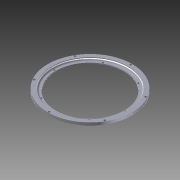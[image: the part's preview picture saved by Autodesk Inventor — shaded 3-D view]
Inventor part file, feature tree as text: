
AUTODESK INVENTOR PART (.ipt)
format: ipt  version: 2014 SP1 (Build 180222100, 222)  size: 822,272 bytes
history: native  units: in
note: dims shown in document units (in); Inventor stores cm internally (conversion verified against a paired STEP export)
features: other x7, plane x5
ambient origin geometry x8: Origin, YZ Plane, XZ Plane, XY Plane, X Axis, Y Axis, Z Axis, Center Point
bodies: Body1 (feature_tree), Body2 (feature_tree), Body3 (feature_tree), Body4 (feature_tree), Body5 (feature_tree), Body6 (feature_tree), Body7 (feature_tree), Body8 (feature_tree), Body9 (feature_tree), Body10 (feature_tree), Body11 (feature_tree), Body12 (feature_tree), Body13 (feature_tree), Body14 (feature_tree), Body15 (feature_tree), Body16 (feature_tree), Body17 (feature_tree), Body18 (feature_tree), Body19 (feature_tree), Body20 (feature_tree), Body21 (feature_tree), Body22 (feature_tree), Body23 (feature_tree), Body24 (feature_tree), Body25 (feature_tree), Body26 (feature_tree), Body27 (feature_tree), Body28 (feature_tree), Body29 (feature_tree), Body30 (feature_tree), Body31 (feature_tree), Body32 (feature_tree), Body33 (feature_tree), Body34 (feature_tree), Body35 (feature_tree), Body36 (feature_tree), Body37 (feature_tree), Body38 (feature_tree), Body39 (feature_tree), Body40 (feature_tree), Body41 (feature_tree), Body42 (feature_tree), Body43 (feature_tree), Body44 (feature_tree), Body45 (feature_tree), Body46 (feature_tree), Body47 (feature_tree), Body48 (feature_tree), Body49 (feature_tree), Body50 (feature_tree), Body51 (feature_tree), Body52 (feature_tree), Body53 (feature_tree), Body54 (feature_tree), Body55 (feature_tree), Body56 (feature_tree), Body57 (feature_tree), Body58 (feature_tree), Body59 (feature_tree), Body60 (feature_tree), Body61 (feature_tree), Body62 (feature_tree), Body63 (feature_tree), Body64 (feature_tree), Body65 (feature_tree), Body66 (feature_tree), Body67 (feature_tree), Body68 (feature_tree), Body69 (feature_tree), Body70 (feature_tree), Body71 (feature_tree), Body72 (feature_tree), Body73 (feature_tree), Body74 (feature_tree), Body75 (feature_tree), Body76 (feature_tree), Body77 (feature_tree), Body78 (feature_tree), Body79 (feature_tree), Body80 (feature_tree), Body81 (feature_tree), Body82 (feature_tree), Body83 (feature_tree), Body84 (feature_tree), Body85 (feature_tree), Body86 (feature_tree), Body87 (feature_tree), Body88 (feature_tree), Body89 (feature_tree), Body90 (feature_tree), Body91 (feature_tree), Body92 (feature_tree), Body93 (feature_tree), Body94 (feature_tree), Body95 (feature_tree), Body96 (feature_tree), Body97 (feature_tree), Body98 (feature_tree), Body99 (feature_tree), Body100 (feature_tree), Body101 (feature_tree), Body102 (feature_tree), Body103 (feature_tree), Body104 (feature_tree), Body105 (feature_tree), Body106 (feature_tree), Body107 (feature_tree), Body108 (feature_tree), Body109 (feature_tree), Body110 (feature_tree), Body111 (feature_tree), Body112 (feature_tree), Body113 (feature_tree), Body114 (feature_tree), Body115 (feature_tree), Body116 (feature_tree), Body117 (feature_tree), Body118 (feature_tree), Body119 (feature_tree), Body120 (feature_tree), Body121 (feature_tree), Body122 (feature_tree), Body123 (feature_tree), Body124 (feature_tree), Body125 (feature_tree), Body126 (feature_tree), Body127 (feature_tree)
feature tree (12):
  other  "Lazy Susan.IGS1"
  other  "Work Axis3"
  other  "Work Axis4"
  other  "Work Axis5"
  other  "Work Axis6"
  plane  "Work Plane4"
  plane  "Work Plane5"
  plane  "Work Plane6"
  plane  "Work Plane2"
  plane  "Work Plane3"
  other  "Composite1"
  other  "Srf1"
